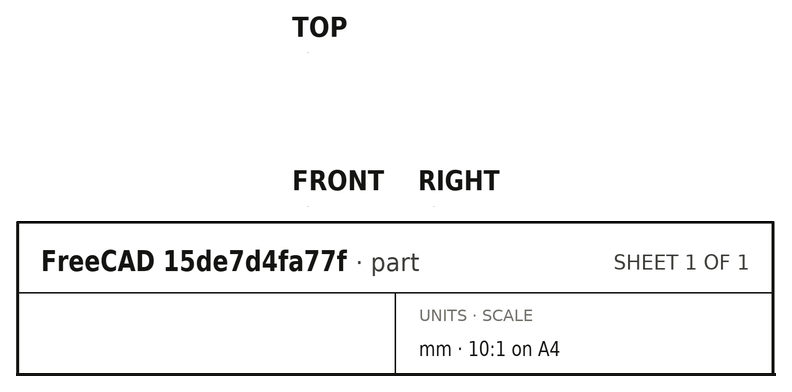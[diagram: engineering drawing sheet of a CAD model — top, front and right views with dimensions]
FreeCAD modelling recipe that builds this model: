
FCSTD DOCUMENT  (FreeCAD 0.21R33694 (Git))
Label: diffPair
License: All rights reserved
LicenseURL: http://en.wikipedia.org/wiki/All_rights_reserved
objects: Part::Part2DObjectPython×23, App::FeaturePython×12, Part::Extrusion×5, Part::Cut×3, Part::FeaturePython×2
note: 33 computed .brp shape members not serialized (recipe doc carries the construction recipe); baked Part::Feature solids carry a one-line shape summary decoded from their .brp

FEATURE [Part::Part2DObjectPython] Wire  # Draft 2D object (typed FeaturePython)
  Area = 0.0014181
  ChamferSize = 0
  Closed = true
  End = (-0.05,0,0)
  FilletRadius = 0
  Length = 0.221006
  MakeFace = true
  Placement = pos=(-0.15,0,0) rot=(0,0,1;0rad)
  Points = (4) [(0,0,0),(0.00545955,0.015,0),(0.0945402,0.015,0),(0.1,-6.12323e-18,0)]
  Start = (-0.15,0,0)
  Subdivisions = 0
FEATURE [Part::Part2DObjectPython] Wire001  # Draft 2D object (typed FeaturePython)
  Area = 0.0014181
  ChamferSize = 0
  Closed = true
  End = (0.15,0,0)
  FilletRadius = 0
  Length = 0.221006
  MakeFace = true
  Placement = pos=(0.05,0,0) rot=(0,0,1;0rad)
  Points = (4) [(0,0,0),(0.00545955,0.015,0),(0.0945402,0.015,0),(0.1,-6.12323e-18,0)]
  Start = (0.05,0,0)
  Subdivisions = 0
FEATURE [Part::Part2DObjectPython] Rectangle  # Draft 2D object (typed FeaturePython)
  Area = 0.13
  ChamferSize = 0
  Columns = 1
  FilletRadius = 0
  Height = 0.1
  Length = 1.3
  MakeFace = true
  Placement = pos=(-0.65,-0.1,0) rot=(0,0,1;0rad)
  Rows = 1
FEATURE [Part::Part2DObjectPython] Rectangle001  # Draft 2D object (typed FeaturePython)
  Area = 0.13
  ChamferSize = 0
  Columns = 1
  FilletRadius = 0
  Height = 0.1
  Length = 1.3
  MakeFace = true
  Placement = pos=(-0.65,0,0) rot=(0,0,1;0rad)
  Rows = 1
FEATURE [Part::Part2DObjectPython] Clone2D  label="Wire (2D)"  # Draft 2D object (typed FeaturePython)
  Fuse = false
  Objects = -> [Wire]
  Placement = pos=(-0.15,0,0) rot=(0,0,1;0rad)
  Scale = (1,1,1)
FEATURE [Part::Part2DObjectPython] Clone2D001  label="Wire001 (2D)"  # Draft 2D object (typed FeaturePython)
  Fuse = false
  Objects = -> [Wire001]
  Placement = pos=(0.05,0,0) rot=(0,0,1;0rad)
  Scale = (1,1,1)
FEATURE [Part::Part2DObjectPython] Clone2D002  label="Rectangle (2D)"  # Draft 2D object (typed FeaturePython)
  Fuse = false
  Objects = -> [Rectangle]
  Placement = pos=(-0.65,-0.1,0) rot=(0,0,1;0rad)
  Scale = (1,1,1)
FEATURE [Part::Part2DObjectPython] Clone2D003  label="Rectangle001 (2D)"  # Draft 2D object (typed FeaturePython)
  Fuse = false
  Objects = -> [Rectangle001]
  Placement = pos=(-0.65,0,0) rot=(0,0,1;0rad)
  Scale = (1,1,1)
FEATURE [Part::Part2DObjectPython] Clone2D004  label="Wire (2D)001"  # Draft 2D object (typed FeaturePython)
  Fuse = false
  Objects = -> [Wire]
  Placement = pos=(-0.15,0,0) rot=(0,0,1;0rad)
  Scale = (1,1,1)
FEATURE [Part::Part2DObjectPython] Clone2D005  label="Wire001 (2D)001"  # Draft 2D object (typed FeaturePython)
  Fuse = false
  Objects = -> [Wire001]
  Placement = pos=(0.05,0,0) rot=(0,0,1;0rad)
  Scale = (1,1,1)
FEATURE [Part::Part2DObjectPython] Clone2D006  label="Rectangle (2D)001"  # Draft 2D object (typed FeaturePython)
  Fuse = false
  Objects = -> [Rectangle]
  Placement = pos=(-0.65,-0.1,0) rot=(0,0,1;0rad)
  Scale = (1,1,1)
FEATURE [Part::Part2DObjectPython] Clone2D007  label="Rectangle001 (2D)001"  # Draft 2D object (typed FeaturePython)
  Fuse = false
  Objects = -> [Rectangle001]
  Placement = pos=(-0.65,0,0) rot=(0,0,1;0rad)
  Scale = (1,1,1)
FEATURE [Part::Extrusion] Extrude004
  Base = -> Clone2D
  Dir = (0,0,1)
  DirMode = 2
  FaceMakerClass = Part::FaceMakerBullseye
  LengthFwd = 2
  LengthRev = 0
  Solid = false
  Symmetric = false
FEATURE [Part::Extrusion] Extrude005
  Base = -> Clone2D001
  Dir = (0,0,1)
  DirMode = 2
  FaceMakerClass = Part::FaceMakerBullseye
  LengthFwd = 2
  LengthRev = 0
  Solid = false
  Symmetric = false
FEATURE [Part::Extrusion] Extrude006
  Base = -> Clone2D002
  Dir = (0,0,1)
  DirMode = 2
  FaceMakerClass = Part::FaceMakerBullseye
  LengthFwd = 2
  LengthRev = 0
  Solid = false
  Symmetric = false
FEATURE [Part::Extrusion] Extrude007
  Base = -> Clone2D003
  Dir = (0,0,1)
  DirMode = 2
  FaceMakerClass = Part::FaceMakerBullseye
  LengthFwd = 2
  LengthRev = 0
  Solid = false
  Symmetric = false
FEATURE [Part::Cut] Cut002
  Base = -> Extrude007
  Tool = -> Extrude004
FEATURE [Part::Cut] Cut003
  Base = -> Cut002
  Tool = -> Extrude005
FEATURE [App::FeaturePython] Text010  label="_Sin(PV){port1}"  # WARN: FeaturePython — macro-defined, semantics opaque (R4)
  Placement = pos=(5.00075,-5.09743,10) rot=(0,0,1;0rad)
  Text = .
FEATURE [App::FeaturePython] Text011  label="_Sout(PV){port2}"  # WARN: FeaturePython — macro-defined, semantics opaque (R4)
  Placement = pos=(5.00075,-5.09743,10) rot=(0,0,1;0rad)
  Text = .
FEATURE [App::FeaturePython] Text012  label="_Lin(1,voltage,in1){v11}"  # WARN: FeaturePython — macro-defined, semantics opaque (R4)
  Placement = pos=(5.00075,-5.09743,10) rot=(0,0,1;0rad)
  Text = .
FEATURE [App::FeaturePython] Text013  label="_Lin(1,current,in1){i11}"  # WARN: FeaturePython — macro-defined, semantics opaque (R4)
  Placement = pos=(5.00075,-5.09743,10) rot=(0,0,1;0rad)
  Text = .
FEATURE [App::FeaturePython] Text014  label="_Lin(2,voltage,in2){v12}"  # WARN: FeaturePython — macro-defined, semantics opaque (R4)
  Placement = pos=(5.00075,-5.09743,10) rot=(0,0,1;0rad)
  Text = .
FEATURE [App::FeaturePython] Text015  label="_Lin(2,current,in2){i12}"  # WARN: FeaturePython — macro-defined, semantics opaque (R4)
  Placement = pos=(5.00075,-5.09743,10) rot=(0,0,1;0rad)
  Text = .
FEATURE [App::FeaturePython] Text016  label="_Lout(3,voltage,out3){v21}"  # WARN: FeaturePython — macro-defined, semantics opaque (R4)
  Placement = pos=(5.00075,-5.09743,10) rot=(0,0,1;0rad)
  Text = .
FEATURE [App::FeaturePython] Text017  label="_Lout(3,current,out3){i21}"  # WARN: FeaturePython — macro-defined, semantics opaque (R4)
  Placement = pos=(5.00075,-5.09743,10) rot=(0,0,1;0rad)
  Text = .
FEATURE [App::FeaturePython] Text018  label="_Lout(4,voltage,out4){v22}"  # WARN: FeaturePython — macro-defined, semantics opaque (R4)
  Placement = pos=(5.00075,-5.09743,10) rot=(0,0,1;0rad)
  Text = .
FEATURE [App::FeaturePython] Text019  label="_Lout(4,current,out4){i22}"  # WARN: FeaturePython — macro-defined, semantics opaque (R4)
  Placement = pos=(5.00075,-5.09743,10) rot=(0,0,1;0rad)
  Text = .
FEATURE [Part::Part2DObjectPython] Wire006  label="_Pi22"  # Draft 2D object (typed FeaturePython)
  Area = 1.4181e-09
  ChamferSize = 0
  Closed = true
  End = (5e-05,-0.0999,4.995)
  FilletRadius = 0
  Length = 0.000221006
  MakeFace = true
  Placement = pos=(0.00015,-0.0999,4.995) rot=(0.707107,0.707107,0;3.14159rad)
  Points = (4) [(0,0,0),(1.5e-05,-5.45983e-06,0),(1.5e-05,-9.45404e-05,0),(0,-0.0001,0)]
  Start = (0.00015,-0.0999,4.995)
  Subdivisions = 0
FEATURE [Part::Part2DObjectPython] Wire007  label="_Pi21"  # Draft 2D object (typed FeaturePython)
  Area = 1.4181e-09
  ChamferSize = 0
  Closed = true
  End = (-0.00015,-0.0999,4.995)
  FilletRadius = 0
  Length = 0.000221006
  MakeFace = true
  Placement = pos=(-5e-05,-0.0999,4.995) rot=(0.707107,0.707107,0;3.14159rad)
  Points = (4) [(0,0,0),(1.5e-05,-5.45983e-06,0),(1.5e-05,-9.45404e-05,0),(0,-0.0001,0)]
  Start = (-5e-05,-0.0999,4.995)
  Subdivisions = 0
FEATURE [Part::Part2DObjectPython] Wire008  label="_Pi11"  # Draft 2D object (typed FeaturePython)
  Area = 1.4181e-09
  ChamferSize = 0
  Closed = true
  End = (-5e-05,-0.0999,4.997)
  FilletRadius = 0
  Length = 0.000221006
  MakeFace = true
  Placement = pos=(-0.00015,-0.0999,4.997) rot=(0,0,1;0rad)
  Points = (4) [(0,0,0),(5.45955e-06,1.5e-05,0),(9.45402e-05,1.5e-05,0),(0.0001,0,0)]
  Start = (-0.00015,-0.0999,4.997)
  Subdivisions = 0
FEATURE [Part::Part2DObjectPython] Wire009  label="_Pi12"  # Draft 2D object (typed FeaturePython)
  Area = 1.4181e-09
  ChamferSize = 0
  Closed = true
  End = (0.00015,-0.0999,4.997)
  FilletRadius = 0
  Length = 0.000221006
  MakeFace = true
  Placement = pos=(5e-05,-0.0999,4.997) rot=(0,0,1;0rad)
  Points = (4) [(0,0,0),(5.45955e-06,1.5e-05,0),(9.45402e-05,1.5e-05,0),(0.0001,0,0)]
  Start = (5e-05,-0.0999,4.997)
  Subdivisions = 0
FEATURE [Part::Part2DObjectPython] Rectangle013  label="_Pport1"  # Draft 2D object (typed FeaturePython)
  Area = 2.6e-07
  ChamferSize = 0
  Columns = 1
  FilletRadius = 0
  Height = 0.0002
  Length = 0.0013
  MakeFace = true
  Placement = pos=(-0.00065,-0.1,4.997) rot=(0,0,1;0rad)
  Rows = 1
FEATURE [Part::Part2DObjectPython] Line  label="_Pv11"  # Draft 2D object (typed FeaturePython)
  Area = 0
  ChamferSize = 0
  Closed = false
  End = (-0.0001,-0.0999,4.997)
  FilletRadius = 0
  Length = 0.0001
  MakeFace = true
  Placement = pos=(0,-0.1,4.997) rot=(0,0,1;0rad)
  Points = (2) [(-0.0001,0,0),(-0.0001,0.0001,0)]
  Start = (-0.0001,-0.1,4.997)
  Subdivisions = 0
FEATURE [Part::Part2DObjectPython] Line004  label="_Pv12"  # Draft 2D object (typed FeaturePython)
  Area = 0
  ChamferSize = 0
  Closed = false
  End = (0.0001,-0.0999,4.997)
  FilletRadius = 0
  Length = 0.0001
  MakeFace = true
  Placement = pos=(0,-0.1,4.997) rot=(0,0,1;0rad)
  Points = (2) [(0.0001,0,0),(0.0001,0.0001,0)]
  Start = (0.0001,-0.1,4.997)
  Subdivisions = 0
FEATURE [Part::Part2DObjectPython] Rectangle014  label="_Pport2"  # Draft 2D object (typed FeaturePython)
  Area = 2.6e-07
  ChamferSize = 0
  Columns = 1
  FilletRadius = 0
  Height = 0.0013
  Length = 0.0002
  MakeFace = true
  Placement = pos=(-0.00065,-0.1,4.995) rot=(0.707107,0.707107,0;3.14159rad)
  Rows = 1
FEATURE [Part::Part2DObjectPython] Line005  label="_Pv21"  # Draft 2D object (typed FeaturePython)
  Area = 0
  ChamferSize = 0
  Closed = false
  End = (-0.0001,-0.0999,4.995)
  FilletRadius = 0
  Length = 0.0001
  MakeFace = true
  Placement = pos=(0,-0.1,4.995) rot=(0.707107,0.707107,0;3.14159rad)
  Points = (2) [(1.38778e-17,-0.0001,0),(0.0001,-0.0001,0)]
  Start = (-0.0001,-0.1,4.995)
  Subdivisions = 0
FEATURE [Part::Part2DObjectPython] Line006  label="_Pv22"  # Draft 2D object (typed FeaturePython)
  Area = 0
  ChamferSize = 0
  Closed = false
  End = (0.0001,-0.0999,4.995)
  FilletRadius = 0
  Length = 0.0001
  MakeFace = true
  Placement = pos=(0,-0.1,4.995) rot=(0.707107,0.707107,0;3.14159rad)
  Points = (2) [(1.38778e-17,0.0001,0),(0.0001,0.0001,0)]
  Start = (0.0001,-0.1,4.995)
  Subdivisions = 0
FEATURE [Part::Part2DObjectPython] Rectangle015  # Draft 2D object (typed FeaturePython)
  Area = 0.01
  ChamferSize = 0
  Columns = 1
  FilletRadius = 0
  Height = 0.1
  Length = 0.1
  MakeFace = true
  Placement = pos=(-0.15,0,2.45) rot=(1,0,0;1.5708rad)
  Rows = 1
FEATURE [Part::Extrusion] Extrude
  Base = -> Rectangle015
  Dir = (0,-1,2e-16)
  DirMode = 2
  FaceMakerClass = Part::FaceMakerBullseye
  LengthFwd = 0.1
  LengthRev = 0
  Placement = pos=(0,0,-1.5) rot=(0,0,1;0rad)
  Solid = false
  Symmetric = false
FEATURE [Part::Cut] Cut
  Base = -> Extrude006
  Tool = -> Extrude
FEATURE [Part::FeaturePython] BooleanFragments  # WARN: FeaturePython — macro-defined, semantics opaque (R4)
  Mode = 0
  Objects = -> [Cut003,Cut]
  Tolerance = 0
FEATURE [Part::FeaturePython] Clone  label="scaled"  # Draft clone (typed FeaturePython)
  AttacherType = Attacher::AttachEngine3D
  Fuse = false
  Objects = -> [BooleanFragments]
  Placement = pos=(0,-0.0999,4.995) rot=(0,0,1;0rad)
  Scale = (0.001,0.001,0.001)
FEATURE [App::FeaturePython] Text020  label="_D(1,2)"  # WARN: FeaturePython — macro-defined, semantics opaque (R4)
  Placement = pos=(5.00075,-5.09743,10) rot=(0,0,1;0rad)
  Text = .
FEATURE [App::FeaturePython] Text021  label="_D(3,4)"  # WARN: FeaturePython — macro-defined, semantics opaque (R4)
  Placement = pos=(5.00075,-5.09743,10) rot=(0,0,1;0rad)
  Text = .
